# Revit family: 3-656-xx - Spindle Pendant
name_source: partatom
category: Luminarias
units: mm (PartAtom-declared; Revit-internal decimal feet)

## family parameters
Anfitrión = Techo
Compartido = No
Corte con vacíos al cargar = No
Cota de conector redondo = Diámetro de uso
Número OmniClass = 23.80.70.11
Origen de luz = Sí
Punto de cálculo de habitación = No
Siempre vertical = Sí
Tipo de pieza = Normal
Título OmniClass = Luminaries for Internal Lighting

## types (1)
- 3-656-114 / Polished Chrome - Transparent Glass
    Archivo de red fotométrica = 3-656 Spindle Pendant.ies
    Cambio de temperatura de color de luz atenuada = <Ninguno>
    Comentarios de vataje = 6.57 W at 120 V
    Elevación por defecto = 0 "
    Fabricante = Oxygen Lighting and Fans
    Filtro de color = 16777215
    Glass = White Opal Glass
    Lámpara = LED Array
    Main Diffuser = Matte White Acrylic
    Metal Finish = 14 - Polished Chrome
    Modelo = 3-xxx-xx / Pendant
    References = Ref. 3 = 120 V / Ref. 37 = 277 V
    URL = www.oxygenlighting.com
    Voltage = 120 V
    Voltage Input = 120 V or 277 V - 50/60 Hz
    Ángulo de inclinación = 90.00°

## geometry (parser evidence)
native form markers: Sweep x5
no freeform markers — native parametric forms only
